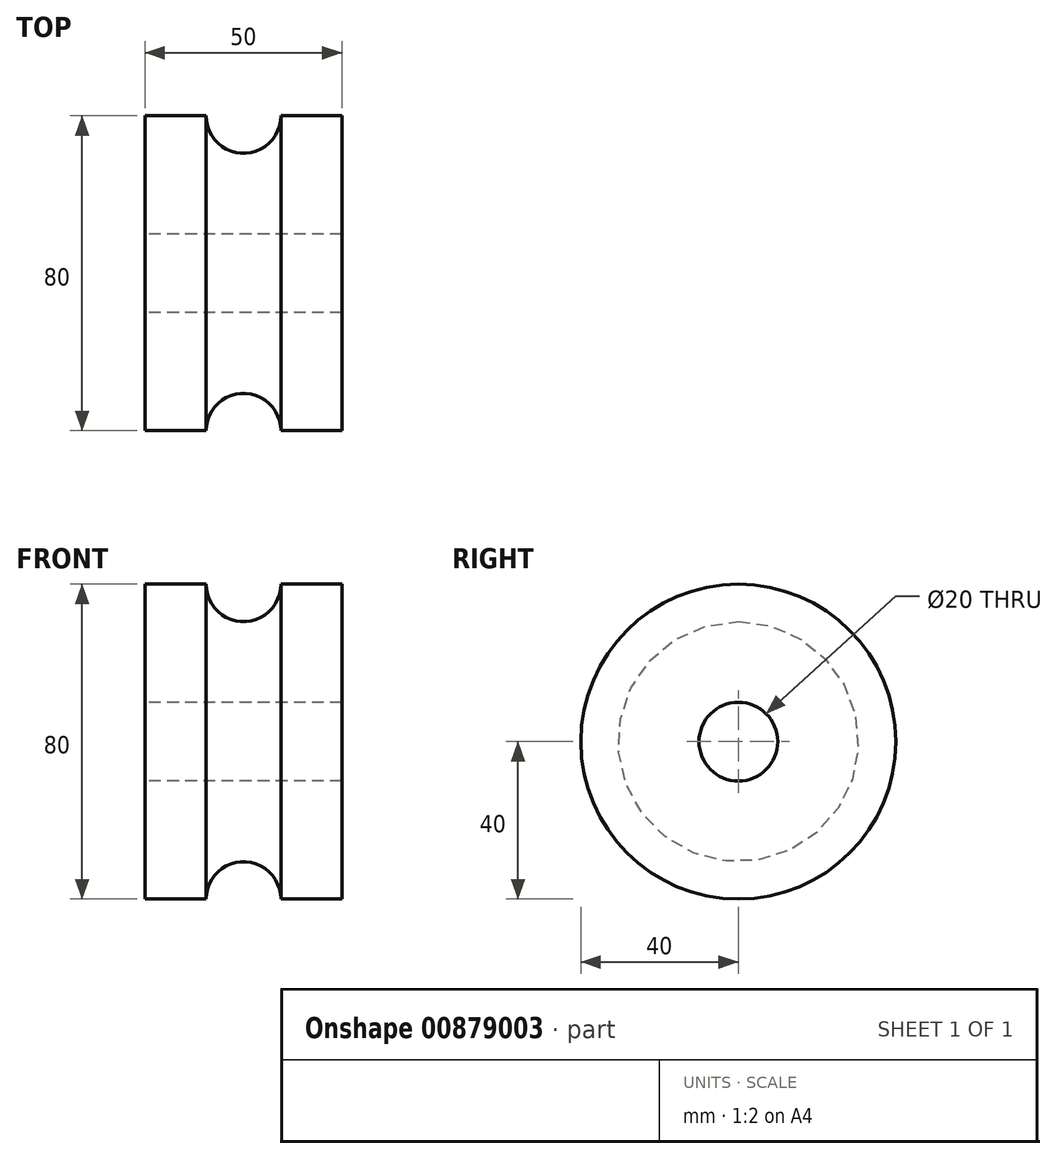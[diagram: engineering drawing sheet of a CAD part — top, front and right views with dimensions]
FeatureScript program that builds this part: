
annotation { "Feature Type Name" : "Feature", "Feature Type Description" : "" }
export const myFeature = defineFeature(function(context is Context, id is Id, definition is map)
    precondition{}
    {
        {
            var Q0;
            Q0=qCreatedBy(makeId("Front.planeOp"),FACE);
            var sketch = newSketch(context, id + "F0", { "sketchPlane" : qUnion([Q0])});
            skLineSegment(sketch, "E0", {"start": v(-25, 40) * mm, "end": v(-9.5, 40) * mm});
            skLineSegment(sketch, "E1", {"start": v(-25, 10) * mm, "end": v(0, 10) * mm});
            skLineSegment(sketch, "E2", {"start": v(0, 10) * mm, "end": v(0, 40) * mm});
            skLineSegment(sketch, "E3", {"start": v(0, 0) * mm, "end": v(0, 10) * mm, "construction": true});
            skLineSegment(sketch, "E4", {"start": v(-25, 10) * mm, "end": v(-25, 0) * mm, "construction": true});
            skLineSegment(sketch, "E5", {"start": v(-25, 0) * mm, "end": v(0, 0) * mm, "construction": true});
            skLineSegment(sketch, "E6", {"start": v(-25, 40) * mm, "end": v(-25, 10) * mm});
            skLineSegment(sketch, "E7", {"start": v(0, 40) * mm, "end": v(0, 10) * mm, "construction": true});
            skLineSegment(sketch, "E8.MirrorCS", {"start": v(25, 40) * mm, "end": v(9.5, 40) * mm});
            skLineSegment(sketch, "E9.MirrorCS", {"start": v(25, 40) * mm, "end": v(25, 10) * mm});
            skLineSegment(sketch, "E10.MirrorCS", {"start": v(25, 10) * mm, "end": v(0, 10) * mm});
            skArc(sketch, "E11", {"start": v(-9.5, 40) * mm, "mid": v(0, 30.5) * mm, "end": v(9.5, 40) * mm});
            skSolve(sketch);
        }
        {
            var Q0;
            {var subQ4=sQuery(id+"F0.wireOp",EDGE,"E0");Q0=makeQuery(id+"F0.imprint","IMPRINT",FACE,{"disambiguationData":[TD([[makeQuery(id+"F0.imprint","IMPRINT",EDGE,{"derivedFrom":subQ4}),-1.0]])]});}
            var Q1;
            {var subQ1=sQuery(id+"F0.wireOp",EDGE,"E8.MirrorCS");Q1=makeQuery(id+"F0.imprint","IMPRINT",FACE,{"disambiguationData":[TD([[makeQuery(id+"F0.imprint","IMPRINT",EDGE,{"derivedFrom":subQ1}),1.0]])]});}
            var Q2;
            Q2=sQuery(id+"F0.wireOp",EDGE,"E5");
            revolve(context, id + "F1", {"surfaceOperationType" : NewSurfaceOperationType.NEW, "entities" : qUnion([Q0, Q1]), "axis" : qUnion([Q2]), "revolveType" : RevolveType.FULL});
        }
    });
